# Revit family: 5in_Round_Xicato-P5
name_source: partatom
category: Lighting Fixtures
revit_build: Autodesk Revit 2014 (Build: 20130308_1515(x64)
units: mm (PartAtom-declared; Revit-internal decimal feet)

## types (9) — shared parameters
Assembly Code = D5020210
Backbox = Hubbell-White
Color Filter = 16777215
Default Elevation = 48.000"
Description = Narrow, Medium, Wide Distribution Downlights.
Dimming Lamp Color Temperature Shift = <None>
Emit Shape Visible in Rendering = No
Emit from Circle Diameter = 4.000"
Glass = Hubbell-White Glass
Lamp = LED Lamp
Load Classification = Lighting
Manufacturer = Kurt Versen
Model = 5in Round Xicato XTM Surface Forms-Pendant Mount (P5)
Power Factor = 0.9
Product Documentation Link = https://hubbellcdn.com
Product Page URL = https://www.hubbell.com
Tilt Angle = -90.00°
URL = https://www.hubbell.com
Voltage = 120 V
Warranty = 5 Year Warranty
Wattage Comments = 12W,17W,25W

## per-type parameters (varying)
| type | Apparent Load | Beam Spread | Photometric Web File | Watts |
| L332_12W_Xicato_XTM_1100_lm_3000K | 13 VA | Wide | L332_12W_Xicato_XTM_1100_lm_3000K.IES | 12 W |
| L332_17W_Xicato_XTM_1500_lm_3000K | 19 VA | Wide | L332_17W_Xicato_XTM_1500_lm_3000K.IES | 17 W |
| L332_25W_Xicato_XTM_2100_lm_3000K | 28 VA | Wide | L332_25W_Xicato_XTM_2100_lm_3000K.IES | 25 W |
| L334_17W_Xicato_XTM_1500_lm_3000K | 19 VA | Medium | L334_17W_Xicato_XTM_1500_lm_3000K.IES | 17 W |
| L334_12W_Xicato_XTM_1100_lm_3000K | 13 VA | Medium | L334_12W_Xicato_XTM_1100_lm_3000K.IES | 12 W |
| L334_25W_Xicato_XTM_2100_lm_3000K | 28 VA | Medium | L334_25W_Xicato_XTM_2100_lm_3000K.IES | 25 W |
| L336_12W_Xicato_XTM_1100_lm_3000K | 13 VA | Narrow | L336_12W_Xicato_XTM_1100_lm_3000K.IES | 12 W |
| L336_17W_Xicato_XTM_1500_lm_3000K | 19 VA | Narrow | L336_17W_Xicato_XTM_1500_lm_3000K.IES | 17 W |
| L336_25W_Xicato_XTM_2100_lm_3000K | 28 VA | Narrow | L336_25W_Xicato_XTM_2100_lm_3000K.IES | 25 W |

## geometry (parser evidence)
native form markers: Blend x4, Sweep x3
no freeform markers — native parametric forms only
